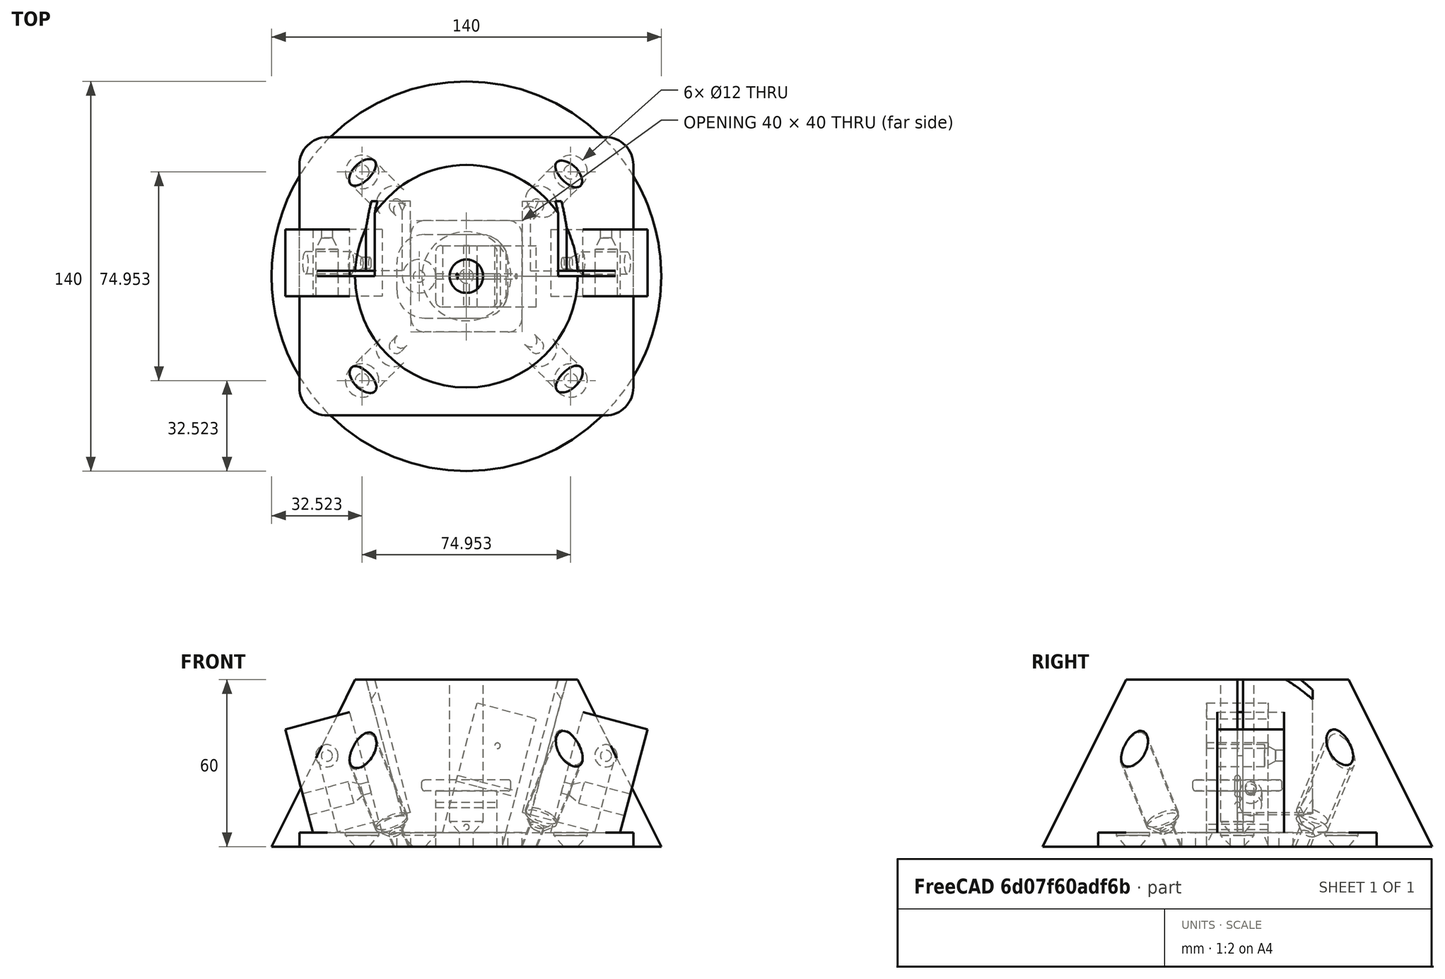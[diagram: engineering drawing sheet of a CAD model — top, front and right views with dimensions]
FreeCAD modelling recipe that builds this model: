
FCSTD DOCUMENT  (FreeCAD 0.18.4R)
Label: glove_holder
License: All rights reserved
LicenseURL: http://en.wikipedia.org/wiki/All_rights_reserved
objects: Part::MultiFuse×15, Part::Cylinder×14, Part::Box×9, PartDesign::FeatureBase×9, PartDesign::Body×9, Part::Cut×6, Part::Fillet×5, Part::Cone×4, Part::Mirroring×2, Part::FeaturePython×2
note: 75 computed .brp shape members not serialized (recipe doc carries the construction recipe); baked Part::Feature solids carry a one-line shape summary decoded from their .brp

FEATURE [Part::Cone] Cone
  Angle = 360
  AttacherType = Attacher::AttachEngine3D
  Height = 60
  Radius1 = 70
  Radius2 = 40
FEATURE [Part::Box] Box  label="Cube"
  AttacherType = Attacher::AttachEngine3D
  Height = 300
  Length = 3
  Width = 27
FEATURE [Part::Box] Box001  label="Cube001"
  AttacherType = Attacher::AttachEngine3D
  Height = 300
  Length = 27
  Width = 2
FEATURE [Part::MultiFuse] Fusion  label="bracket"
  Placement = pos=(20.1704,0,12.2941) rot=(0,1,0;0.261799rad)
  Shapes = -> [Box,Box001]
FEATURE [Part::Mirroring] Part__Mirroring  label="bracket (Mirror #1)"
  Base = (0,0,0)
  Normal = (1,0,0)
  Source = -> Fusion
FEATURE [Part::Cylinder] Cylinder
  Angle = 360
  AttacherType = Attacher::AttachEngine3D
  Height = 60
  Placement = pos=(0,0,4) rot=(0,0,1;0rad)
  Radius = 6
FEATURE [Part::Cone] Cone001
  Angle = 360
  AttacherType = Attacher::AttachEngine3D
  Height = 4
  Radius1 = 2.5
  Radius2 = 6
FEATURE [Part::Cylinder] Cylinder001
  Angle = 360
  AttacherType = Attacher::AttachEngine3D
  Height = 40
  Placement = pos=(0,0,-40) rot=(0,0,1;0rad)
  Radius = 2.5
FEATURE [Part::MultiFuse] Fusion002  label="screw hole fusion"
  Placement = pos=(0,0,5) rot=(0,0,1;0rad)
  Shapes = -> [Cylinder001,Cone001,Cylinder]
FEATURE [PartDesign::FeatureBase] Clone
  BaseFeature = -> Fusion002
FEATURE [PartDesign::Body] Body  label="base screw hole fusion clone"
  BaseFeature = -> Fusion002
  Group = -> [Clone]
  Origin = -> Origin
  Placement = pos=(0,35.9455,4.65064) rot=(-1,0,0;0.523599rad)
  Tip = -> Clone
FEATURE [Part::FeaturePython] Array  label="screw holes fusion array"  # Draft array (typed FeaturePython)
  Angle = 360
  ArrayType = 1
  Axis = (0,0,1)
  Base = -> Body
  Center = (0,0,0)
  Fuse = false
  IntervalAxis = (0,0,1)
  IntervalX = (1,0,0)
  IntervalY = (0,1,0)
  IntervalZ = (0,0,1)
  NumberPolar = 4
  NumberX = 1
  NumberY = 1
  NumberZ = 1
  Placement = pos=(0,0,0) rot=(0,0,1;0.785398rad)
FEATURE [Part::MultiFuse] Fusion001  label="bracket fusion"
  Shapes = -> [Fusion,Part__Mirroring,Array,Fusion002]
FEATURE [Part::Cut] Cut  label="stand cut"
  Base = -> Cone
  Tool = -> Fusion001
FEATURE [Part::Box] Box005  label="Cube005"
  AttacherType = Attacher::AttachEngine3D
  Height = 50
  Length = 24
  Width = 24
FEATURE [Part::Cylinder] Cylinder003  label="base cylinder001"
  Angle = 360
  AttacherType = Attacher::AttachEngine3D
  Height = 20
  Placement = pos=(0,0,-20) rot=(0,0,1;0rad)
  Radius = 70
FEATURE [PartDesign::FeatureBase] Clone001
  BaseFeature = -> Fusion002
  Placement = pos=(0,0,5) rot=(0,0,1;0rad)
FEATURE [PartDesign::Body] Body001  label="screw hole clone"
  BaseFeature = -> Fusion002
  Group = -> [Clone001]
  Origin = -> Origin001
  Placement = pos=(0,0,-5) rot=(0,0,1;0rad)
  Tip = -> Clone001
FEATURE [PartDesign::FeatureBase] Clone002
  BaseFeature = -> Body001
  Placement = pos=(0,0,-5) rot=(0,0,1;0rad)
FEATURE [PartDesign::Body] Body002  label="screw hole clone clone"
  BaseFeature = -> Body001
  Group = -> [Clone002]
  Origin = -> Origin002
  Placement = pos=(0,53,0) rot=(0,0,1;0rad)
  Tip = -> Clone002
FEATURE [Part::FeaturePython] Array001  # Draft array (typed FeaturePython)
  Angle = 360
  ArrayType = 1
  Axis = (0,0,1)
  Base = -> Body002
  Center = (0,0,0)
  Fuse = false
  IntervalAxis = (0,0,0)
  IntervalX = (1,0,0)
  IntervalY = (0,1,0)
  IntervalZ = (0,0,1)
  NumberPolar = 4
  NumberX = 1
  NumberY = 1
  NumberZ = 1
  Placement = pos=(0,0,0) rot=(0,0,1;0.785398rad)
FEATURE [Part::Cylinder] Cylinder004
  Angle = 360
  AttacherType = Attacher::AttachEngine3D
  Height = 60
  Placement = pos=(0,0,4) rot=(0,0,1;0rad)
  Radius = 4
FEATURE [Part::Cone] Cone002
  Angle = 360
  AttacherType = Attacher::AttachEngine3D
  Height = 4
  Radius1 = 2
  Radius2 = 4
FEATURE [Part::Cylinder] Cylinder005
  Angle = 360
  AttacherType = Attacher::AttachEngine3D
  Height = 40
  Placement = pos=(0,0,-40) rot=(0,0,1;0rad)
  Radius = 2
FEATURE [Part::MultiFuse] Fusion007  label="m3 screw hole fusion"
  Placement = pos=(0,0,5) rot=(0,0,1;0rad)
  Shapes = -> [Cylinder005,Cone002,Cylinder004]
FEATURE [PartDesign::FeatureBase] Clone003
  BaseFeature = -> Fusion007
  Placement = pos=(0,0,5) rot=(0,0,1;0rad)
FEATURE [PartDesign::Body] Body003  label="m3 screw hole fusion clone"
  BaseFeature = -> Fusion007
  Group = -> [Clone003]
  Origin = -> Origin003
  Placement = pos=(-2,12,22) rot=(0,1,0;1.5708rad)
  Tip = -> Clone003
FEATURE [PartDesign::FeatureBase] Clone004
  BaseFeature = -> Fusion007
  Placement = pos=(0,0,5) rot=(0,0,1;0rad)
FEATURE [PartDesign::Body] Body004  label="m3 screw hole fusion clone001"
  BaseFeature = -> Fusion007
  Group = -> [Clone004]
  Origin = -> Origin004
  Placement = pos=(12,26,37) rot=(1,0,0;1.5708rad)
  Tip = -> Clone004
FEATURE [Part::MultiFuse] Fusion008  label="m3 hole fusion"
  Shapes = -> [Body003,Body004]
FEATURE [Part::Cut] Cut002  label="cube cut"
  Base = -> Box005
  Placement = pos=(28.9778,-7.23543,0) rot=(0,1,0;0.261799rad)
  Tool = -> Fusion008
FEATURE [Part::Mirroring] Part__Mirroring001  label="bracket (Mirror #1)001"
  Base = (0,7,0)
  Normal = (1,0,0)
  Source = -> Cut002
FEATURE [Part::Box] Box006  label="base cube"
  AttacherType = Attacher::AttachEngine3D
  Height = 5
  Length = 120
  Placement = pos=(-60,-50,0) rot=(0,0,1;0rad)
  Width = 100
FEATURE [Part::Fillet] Fillet  label="base cube fillet"
  Base = -> Box006
  Edges = 4 edges r=10: [Edge1,Edge3,Edge5,Edge7]
FEATURE [Part::MultiFuse] Fusion005
  Shapes = -> [Part__Mirroring001,Cut002,Fillet]
FEATURE [Part::Box] Box007  label="central hole cube"
  AttacherType = Attacher::AttachEngine3D
  Height = 10
  Length = 40
  Placement = pos=(-20,-20,0) rot=(0,0,1;0rad)
  Width = 40
FEATURE [Part::Fillet] Fillet001  label="central hole cube fillet"
  Base = -> Box007
  Edges = 4 edges r=5: [Edge1,Edge3,Edge5,Edge7]
FEATURE [Part::MultiFuse] Fusion006  label="extraction fusion"
  Shapes = -> [Cylinder003,Body001,Array001,Fillet001]
FEATURE [Part::Cut] Cut001  label="stand cut v2"
  Base = -> Fusion005
  Tool = -> Fusion006
FEATURE [Part::Cylinder] Cylinder010
  Angle = 360
  AttacherType = Attacher::AttachEngine3D
  Height = 60
  Placement = pos=(0,0,4) rot=(0,0,1;0rad)
  Radius = 6
FEATURE [Part::Cone] Cone005
  Angle = 360
  AttacherType = Attacher::AttachEngine3D
  Height = 4
  Radius1 = 2.1
  Radius2 = 6
FEATURE [Part::Cylinder] Cylinder011
  Angle = 360
  AttacherType = Attacher::AttachEngine3D
  Height = 40
  Placement = pos=(0,0,-40) rot=(0,0,1;0rad)
  Radius = 2.1
FEATURE [Part::MultiFuse] Fusion012  label="screw hole fusion001"
  Placement = pos=(0,0,5) rot=(0,0,1;0rad)
  Shapes = -> [Cylinder011,Cone005,Cylinder010]
FEATURE [PartDesign::FeatureBase] Clone007
  BaseFeature = -> Fusion012
  Placement = pos=(0,0,5) rot=(0,0,1;0rad)
FEATURE [PartDesign::Body] Body008  label="screw hole clone001"
  BaseFeature = -> Fusion012
  Group = -> [Clone007]
  Origin = -> Origin006
  Placement = pos=(-17,0,-5) rot=(0,0,1;0rad)
  Tip = -> Clone007
FEATURE [Part::Box] Box008  label="Cube006"
  AttacherType = Attacher::AttachEngine3D
  Height = 50
  Length = 22
  Placement = pos=(-7,0,0) rot=(0,0,1;0rad)
  Width = 22
FEATURE [Part::Cylinder] Cylinder013  label="screw hole cylinder001"
  Angle = 360
  AttacherType = Attacher::AttachEngine3D
  Height = 60
  Radius = 1
FEATURE [Part::Cylinder] Cylinder014  label="screw hole cylinder"
  Angle = 360
  AttacherType = Attacher::AttachEngine3D
  Height = 40
  Placement = pos=(0,0,-40) rot=(0,0,1;0rad)
  Radius = 1
FEATURE [Part::MultiFuse] Fusion011  label="m3 screw hole fusion003"
  Placement = pos=(0,0,5) rot=(0,0,1;0rad)
  Shapes = -> [Cylinder014,Cylinder013]
FEATURE [PartDesign::FeatureBase] Clone005
  BaseFeature = -> Fusion011
  Placement = pos=(0,0,5) rot=(0,0,1;0rad)
FEATURE [PartDesign::Body] Body005  label="m3 screw hole fusion clone002"
  BaseFeature = -> Fusion011
  Group = -> [Clone005]
  Origin = -> Origin008
  Placement = pos=(11,26,37) rot=(1,0,0;1.5708rad)
  Tip = -> Clone005
FEATURE [Part::Box] Box009  label="base cube001"
  AttacherType = Attacher::AttachEngine3D
  Height = 5
  Length = 40
  Placement = pos=(-25,-15,0) rot=(0,0,1;0rad)
  Width = 30
FEATURE [Part::Fillet] Fillet002  label="base cube fillet001"
  Base = -> Box009
  Edges = 4 edges r=10: [Edge1,Edge3,Edge5,Edge7]
FEATURE [Part::Box] Box010  label="base cube002"
  AttacherType = Attacher::AttachEngine3D
  Height = 20
  Length = 100
  Placement = pos=(-8,-50,-20) rot=(0,0,1;0rad)
  Width = 100
FEATURE [Part::MultiFuse] Fusion014  label="extraction fusion001"
  Shapes = -> [Body008,Box010]
FEATURE [Part::Cylinder] Cylinder015
  Angle = 360
  AttacherType = Attacher::AttachEngine3D
  Height = 60
  Radius = 1
FEATURE [Part::Cylinder] Cylinder016
  Angle = 360
  AttacherType = Attacher::AttachEngine3D
  Height = 40
  Placement = pos=(0,0,-40) rot=(0,0,1;0rad)
  Radius = 1
FEATURE [Part::MultiFuse] Fusion016  label="screw hole fusion002"
  Placement = pos=(0,0,5) rot=(0,0,1;0rad)
  Shapes = -> [Cylinder016,Cylinder015]
FEATURE [PartDesign::FeatureBase] Clone008
  BaseFeature = -> Fusion016
  Placement = pos=(0,0,5) rot=(0,0,1;0rad)
FEATURE [PartDesign::Body] Body009  label="screw hole clone002"
  BaseFeature = -> Fusion016
  Group = -> [Clone008]
  Origin = -> Origin009
  Placement = pos=(0,0,-5) rot=(0,0,1;0rad)
  Tip = -> Clone008
FEATURE [PartDesign::FeatureBase] Clone006
  BaseFeature = -> Body009
  Placement = pos=(0,0,5) rot=(0,0,1;0rad)
FEATURE [PartDesign::Body] Body006  label="m3 screw hole fusion clone003"
  BaseFeature = -> Body009
  Group = -> [Clone006]
  Origin = -> Origin007
  Placement = pos=(-2,11,22) rot=(0,1,0;1.5708rad)
  Tip = -> Clone006
FEATURE [Part::MultiFuse] Fusion015  label="m3 hole fusion001"
  Placement = pos=(-7,0,0) rot=(0,1,0;0rad)
  Shapes = -> [Body006,Body005]
FEATURE [Part::Cut] Cut003  label="cube cut001"
  Base = -> Box008
  Placement = pos=(-2.27139,-11,1.53433) rot=(0,1,0;0.261799rad)
  Tool = -> Fusion015
FEATURE [Part::MultiFuse] Fusion013
  Shapes = -> [Cut003,Fillet002]
FEATURE [Part::Cut] Cut004  label="stand cut v3"
  Base = -> Fusion013
  Tool = -> Fusion014
FEATURE [Part::Box] Box011  label="top cube"
  AttacherType = Attacher::AttachEngine3D
  Height = 20
  Length = 22
  Placement = pos=(-11,-11,0) rot=(0,0,1;0rad)
  Width = 22
FEATURE [Part::Cylinder] Cylinder017
  Angle = 360
  AttacherType = Attacher::AttachEngine3D
  Height = 4
  Placement = pos=(0,0,20) rot=(0,0,1;0rad)
  Radius = 16
FEATURE [Part::Cylinder] Cylinder018  label="screw hole cylinder002"
  Angle = 360
  AttacherType = Attacher::AttachEngine3D
  Height = 40
  Placement = pos=(-20,0,15) rot=(0,1,0;1.5708rad)
  Radius = 1
FEATURE [Part::Cylinder] Cylinder019  label="screw hole cylinder003"
  Angle = 360
  AttacherType = Attacher::AttachEngine3D
  Height = 40
  Placement = pos=(0,20,7) rot=(0.57735,0.57735,-0.57735;2.0944rad)
  Radius = 1
FEATURE [Part::MultiFuse] Fusion018  label="tope screw hole fusion"
  Shapes = -> [Cylinder018,Cylinder019]
FEATURE [Part::Fillet] Fillet003
  Base = -> Cylinder017
  Edges = 2 edges r=1: [Edge1,Edge3]
FEATURE [Part::Fillet] Fillet004
  Base = -> Box011
  Edges = 4 edges r=2: [Edge1,Edge3,Edge5,Edge7]
FEATURE [Part::MultiFuse] Fusion017  label="top fusion"
  Shapes = -> [Fillet003,Fillet004]
FEATURE [Part::Cut] Cut005  label="top cut"
  Base = -> Fusion017
  Tool = -> Fusion018
